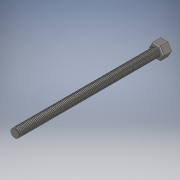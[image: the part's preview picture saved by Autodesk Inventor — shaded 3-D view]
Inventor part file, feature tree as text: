
AUTODESK INVENTOR PART (.ipt)
format: ipt  version: 2019 (Build 230136000, 136)  size: 875,520 bytes
history: native  units: mm
features: sketch x3, extrude x2, helix x1, fillet x1
ambient origin geometry x8: Origin, YZ Plane, XZ Plane, XY Plane, X Axis, Y Axis, Z Axis, Center Point
bodies: Solid1 (feature_tree)
feature tree (7):
  extrude  "Extrusion1"  Depth=118.75mm TaperAngle=0.0deg
  extrude  "Extrusion2"  Depth=7.5mm
  helix  "Coil1"  [1 undecoded]
  fillet  "Fillet1"  Radius=0.5mm
  sketch  "Sketch1"  dims[d0=7.0mm d1=118.75mm d2=0.0mm]
  sketch  "Sketch2"  dims[d3=12.4mm d4=5.369358mm d5=7.5mm d6=0.0mm d7=0.5mm]
  sketch  "Sketch3"  dims[d8=0.5mm d9=10.0mm d10=118.75mm d11=1000.0mm d12=0.0mm d13=90.0deg d14=90.0deg d15=0.0mm d16=0.0mm d17=0.8mm]
note: 1 required parameter value undecoded (feature->parameter linkage not recoverable at this tier; creation-order binding heuristic only, values carry confidence <= 0.55)
